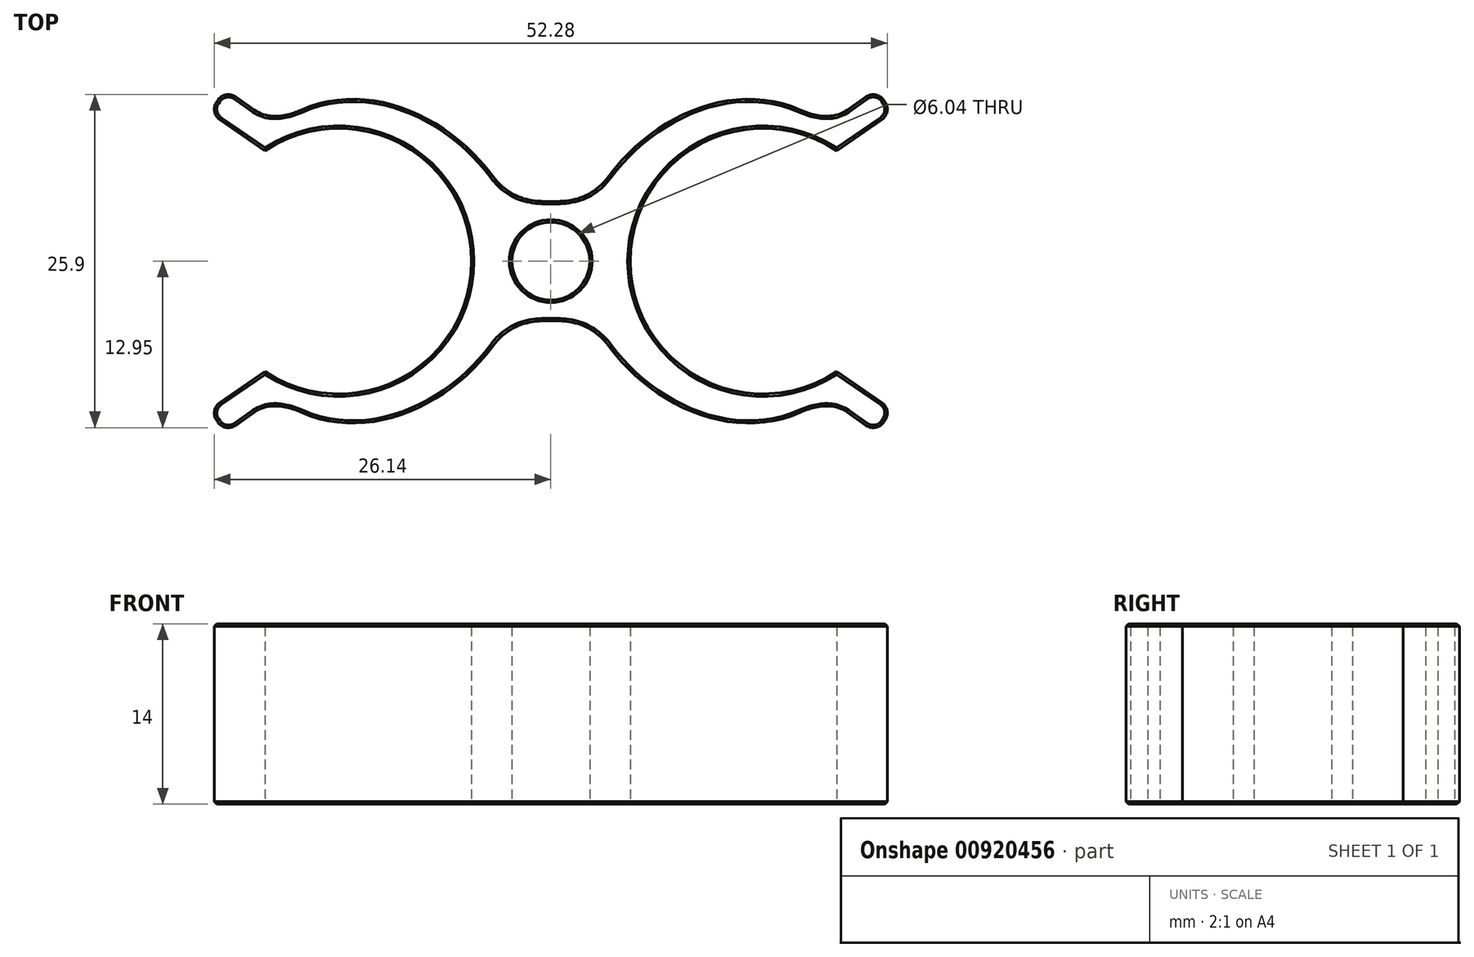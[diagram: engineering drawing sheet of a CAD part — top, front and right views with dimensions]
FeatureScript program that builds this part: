
annotation { "Feature Type Name" : "Feature", "Feature Type Description" : "" }
export const myFeature = defineFeature(function(context is Context, id is Id, definition is map)
    precondition{}
    {
        {
            var Q0;
            Q0=qCreatedBy(makeId("Top.planeOp"),FACE);
            var sketch = newSketch(context, id + "F0", { "sketchPlane" : qUnion([Q0])});
            skLineSegment(sketch, "E0.bottom", {"start": v(-30.7, 16.04) * mm, "end": v(39.3, 16.04) * mm, "construction": true});
            skLineSegment(sketch, "E0.top", {"start": v(-30.7, -18.6) * mm, "end": v(39.3, -18.6) * mm, "construction": true});
            skLineSegment(sketch, "E0.left", {"start": v(-30.7, 16.04) * mm, "end": v(-30.7, -18.6) * mm, "construction": true});
            skLineSegment(sketch, "E0.right", {"start": v(39.3, 16.04) * mm, "end": v(39.3, -18.6) * mm, "construction": true});
            skCircle(sketch, "E1", {"center": v(-16.48, 0) * mm, "radius": 10.32 * mm});
            skLineSegment(sketch, "E2", {"start": v(-26.53, 11.56) * mm, "end": v(-22.21, 8.58) * mm});
            skLineSegment(sketch, "E3", {"start": v(-26.53, 11.56) * mm, "end": v(-25.3, 13.35) * mm});
            skPoint(sketch, "E4.3.internal.snap0", {"position": v(-25.92, 12.45) * mm});
            skFitSpline(sketch, "E5", {"points": [v(-23.04, 11.75) * mm, v(-19.4, 11.75) * mm], "startDerivative": vector(3.9, -2.77) * mm, "endDerivative": vector(1.97, 0.88) * mm});
            skFitSpline(sketch, "E6", {"points": [v(-19.4, 11.75) * mm, v(-4.53, 6.63) * mm], "startDerivative": vector(15.7, 7.01) * mm, "endDerivative": vector(10.41, -14.02) * mm});
            skFitSpline(sketch, "E7", {"points": [v(-4.53, 6.63) * mm, v(0, 4.64) * mm], "startDerivative": vector(4.34, -5.84) * mm, "endDerivative": vector(3.88, 0) * mm});
            skLineSegment(sketch, "E8", {"start": v(-23.04, 11.75) * mm, "end": v(-25.3, 13.35) * mm});
            skLineSegment(sketch, "E9", {"start": v(-41.93, 0) * mm, "end": v(18.12, 0) * mm, "construction": true});
            skLineSegment(sketch, "E10", {"start": v(0, 33.24) * mm, "end": v(0, -36.87) * mm, "construction": true});
            skCircle(sketch, "E11", {"center": v(0, 0) * mm, "radius": 3.02 * mm});
            skLineSegment(sketch, "E12.MirrorCS", {"start": v(26.53, 11.56) * mm, "end": v(22.21, 8.58) * mm});
            skLineSegment(sketch, "E13.MirrorCS", {"start": v(26.53, 11.56) * mm, "end": v(25.3, 13.35) * mm});
            skLineSegment(sketch, "E14.MirrorCS", {"start": v(23.04, 11.75) * mm, "end": v(25.3, 13.35) * mm});
            skFitSpline(sketch, "E15.MirrorCS", {"points": [v(23.04, 11.75) * mm, v(19.4, 11.75) * mm], "startDerivative": vector(-3.9, -2.77) * mm, "endDerivative": vector(-1.97, 0.88) * mm});
            skFitSpline(sketch, "E16.MirrorCS", {"points": [v(19.4, 11.75) * mm, v(4.53, 6.63) * mm], "startDerivative": vector(-15.7, 7.01) * mm, "endDerivative": vector(-10.41, -14.02) * mm});
            skFitSpline(sketch, "E17.MirrorCS", {"points": [v(4.53, 6.63) * mm, v(0, 4.64) * mm], "startDerivative": vector(-4.34, -5.84) * mm, "endDerivative": vector(-3.88, 0) * mm});
            skCircle(sketch, "E18.MirrorC", {"center": v(16.48, 0) * mm, "radius": 10.32 * mm});
            skLineSegment(sketch, "E19.MirrorCS", {"start": v(-26.53, -11.56) * mm, "end": v(-22.21, -8.58) * mm});
            skLineSegment(sketch, "E20.MirrorCS", {"start": v(-26.53, -11.56) * mm, "end": v(-25.3, -13.35) * mm});
            skLineSegment(sketch, "E21.MirrorCS", {"start": v(-23.04, -11.75) * mm, "end": v(-25.3, -13.35) * mm});
            skFitSpline(sketch, "E22.MirrorCS", {"points": [v(-23.04, -11.75) * mm, v(-19.4, -11.75) * mm], "startDerivative": vector(3.9, 2.77) * mm, "endDerivative": vector(1.97, -0.88) * mm});
            skFitSpline(sketch, "E23.MirrorCS", {"points": [v(-19.4, -11.75) * mm, v(-4.53, -6.63) * mm], "startDerivative": vector(15.7, -7.01) * mm, "endDerivative": vector(10.41, 14.02) * mm});
            skFitSpline(sketch, "E24.MirrorCS", {"points": [v(-4.53, -6.63) * mm, v(0, -4.64) * mm], "startDerivative": vector(4.34, 5.84) * mm, "endDerivative": vector(3.88, 0) * mm});
            skFitSpline(sketch, "E25.MirrorCS", {"points": [v(4.53, -6.63) * mm, v(0, -4.64) * mm], "startDerivative": vector(-4.34, 5.84) * mm, "endDerivative": vector(-3.88, 0) * mm});
            skFitSpline(sketch, "E26.MirrorCS", {"points": [v(19.4, -11.75) * mm, v(4.53, -6.63) * mm], "startDerivative": vector(-15.7, -7.01) * mm, "endDerivative": vector(-10.41, 14.02) * mm});
            skFitSpline(sketch, "E27.MirrorCS", {"points": [v(23.04, -11.75) * mm, v(19.4, -11.75) * mm], "startDerivative": vector(-3.9, 2.77) * mm, "endDerivative": vector(-1.97, -0.88) * mm});
            skLineSegment(sketch, "E28.MirrorCS", {"start": v(23.04, -11.75) * mm, "end": v(25.3, -13.35) * mm});
            skLineSegment(sketch, "E29.MirrorCS", {"start": v(26.53, -11.56) * mm, "end": v(25.3, -13.35) * mm});
            skLineSegment(sketch, "E30.MirrorCS", {"start": v(26.53, -11.56) * mm, "end": v(22.21, -8.58) * mm});
            skSolve(sketch);
        }
        {
            var Q0;
            {var subQ4=sQuery(id+"F0.wireOp",EDGE,"E2");Q0=makeQuery(id+"F0.imprint","IMPRINT",FACE,{"disambiguationData":[TD([[makeQuery(id+"F0.imprint","IMPRINT",EDGE,{"derivedFrom":subQ4}),1.0]])]});}
            extrude(context, id + "F1", {"entities" : qUnion([Q0]), "depth" : 14 * mm, "offsetDistance" : 25 * mm});
        }
        {
            var Q0;
            Q0=makeQuery(id+"F1.opExtrude","SWEPT_EDGE",EDGE,{"disambiguationData":[OSD([sQuery(id+"F0.wireOp",EDGE,"E28.MirrorCS"),sQuery(id+"F0.wireOp",EDGE,"E29.MirrorCS")])]});
            var Q1;
            Q1=makeQuery(id+"F1.opExtrude","SWEPT_EDGE",EDGE,{"disambiguationData":[OSD([sQuery(id+"F0.wireOp",EDGE,"E29.MirrorCS"),sQuery(id+"F0.wireOp",EDGE,"E30.MirrorCS")])]});
            var Q2;
            Q2=makeQuery(id+"F1.opExtrude","SWEPT_EDGE",EDGE,{"disambiguationData":[OSD([sQuery(id+"F0.wireOp",EDGE,"E12.MirrorCS"),sQuery(id+"F0.wireOp",EDGE,"E13.MirrorCS")])]});
            var Q3;
            Q3=makeQuery(id+"F1.opExtrude","SWEPT_EDGE",EDGE,{"disambiguationData":[OSD([sQuery(id+"F0.wireOp",EDGE,"E2"),sQuery(id+"F0.wireOp",EDGE,"E3")])]});
            var Q4;
            Q4=makeQuery(id+"F1.opExtrude","SWEPT_EDGE",EDGE,{"disambiguationData":[OSD([sQuery(id+"F0.wireOp",EDGE,"E3"),sQuery(id+"F0.wireOp",EDGE,"E8")])]});
            var Q5;
            Q5=makeQuery(id+"F1.opExtrude","SWEPT_EDGE",EDGE,{"disambiguationData":[OSD([sQuery(id+"F0.wireOp",EDGE,"E20.MirrorCS"),sQuery(id+"F0.wireOp",EDGE,"E21.MirrorCS")])]});
            var Q6;
            Q6=makeQuery(id+"F1.opExtrude","SWEPT_EDGE",EDGE,{"disambiguationData":[OSD([sQuery(id+"F0.wireOp",EDGE,"E19.MirrorCS"),sQuery(id+"F0.wireOp",EDGE,"E20.MirrorCS")])]});
            var Q7;
            Q7=makeQuery(id+"F1.opExtrude","SWEPT_EDGE",EDGE,{"disambiguationData":[OSD([sQuery(id+"F0.wireOp",EDGE,"E13.MirrorCS"),sQuery(id+"F0.wireOp",EDGE,"E14.MirrorCS")])]});
            fillet(context, id + "F2", {"entities" : qUnion([Q0, Q1, Q2, Q3, Q4, Q5, Q6, Q7]), "radius" : 1 * mm, "tangentPropagation" : true, "allowEdgeOverflow" : false});
        }
        {
            var Q0;
            Q0=makeQuery(id+"F1.opExtrude","CAP_FACE",FACE,{"disambiguationData":[OSD([sQuery(id+"F0.wireOp",EDGE,"E1"),sQuery(id+"F0.wireOp",EDGE,"E2"),sQuery(id+"F0.wireOp",EDGE,"E3"),sQuery(id+"F0.wireOp",EDGE,"E5"),sQuery(id+"F0.wireOp",EDGE,"E6"),sQuery(id+"F0.wireOp",EDGE,"E7"),sQuery(id+"F0.wireOp",EDGE,"E8"),sQuery(id+"F0.wireOp",EDGE,"E11"),sQuery(id+"F0.wireOp",EDGE,"E12.MirrorCS"),sQuery(id+"F0.wireOp",EDGE,"E13.MirrorCS"),sQuery(id+"F0.wireOp",EDGE,"E14.MirrorCS"),sQuery(id+"F0.wireOp",EDGE,"E15.MirrorCS"),sQuery(id+"F0.wireOp",EDGE,"E16.MirrorCS"),sQuery(id+"F0.wireOp",EDGE,"E17.MirrorCS"),sQuery(id+"F0.wireOp",EDGE,"E18.MirrorC"),sQuery(id+"F0.wireOp",EDGE,"E19.MirrorCS"),sQuery(id+"F0.wireOp",EDGE,"E20.MirrorCS"),sQuery(id+"F0.wireOp",EDGE,"E21.MirrorCS"),sQuery(id+"F0.wireOp",EDGE,"E22.MirrorCS"),sQuery(id+"F0.wireOp",EDGE,"E23.MirrorCS"),sQuery(id+"F0.wireOp",EDGE,"E24.MirrorCS"),sQuery(id+"F0.wireOp",EDGE,"E25.MirrorCS"),sQuery(id+"F0.wireOp",EDGE,"E26.MirrorCS"),sQuery(id+"F0.wireOp",EDGE,"E27.MirrorCS"),sQuery(id+"F0.wireOp",EDGE,"E28.MirrorCS"),sQuery(id+"F0.wireOp",EDGE,"E29.MirrorCS"),sQuery(id+"F0.wireOp",EDGE,"E30.MirrorCS")])],"isStart":false});
            var Q1;
            Q1=makeQuery(id+"F1.opExtrude","CAP_FACE",FACE,{"disambiguationData":[OSD([sQuery(id+"F0.wireOp",EDGE,"E1"),sQuery(id+"F0.wireOp",EDGE,"E2"),sQuery(id+"F0.wireOp",EDGE,"E3"),sQuery(id+"F0.wireOp",EDGE,"E5"),sQuery(id+"F0.wireOp",EDGE,"E6"),sQuery(id+"F0.wireOp",EDGE,"E7"),sQuery(id+"F0.wireOp",EDGE,"E8"),sQuery(id+"F0.wireOp",EDGE,"E11"),sQuery(id+"F0.wireOp",EDGE,"E12.MirrorCS"),sQuery(id+"F0.wireOp",EDGE,"E13.MirrorCS"),sQuery(id+"F0.wireOp",EDGE,"E14.MirrorCS"),sQuery(id+"F0.wireOp",EDGE,"E15.MirrorCS"),sQuery(id+"F0.wireOp",EDGE,"E16.MirrorCS"),sQuery(id+"F0.wireOp",EDGE,"E17.MirrorCS"),sQuery(id+"F0.wireOp",EDGE,"E18.MirrorC"),sQuery(id+"F0.wireOp",EDGE,"E19.MirrorCS"),sQuery(id+"F0.wireOp",EDGE,"E20.MirrorCS"),sQuery(id+"F0.wireOp",EDGE,"E21.MirrorCS"),sQuery(id+"F0.wireOp",EDGE,"E22.MirrorCS"),sQuery(id+"F0.wireOp",EDGE,"E23.MirrorCS"),sQuery(id+"F0.wireOp",EDGE,"E24.MirrorCS"),sQuery(id+"F0.wireOp",EDGE,"E25.MirrorCS"),sQuery(id+"F0.wireOp",EDGE,"E26.MirrorCS"),sQuery(id+"F0.wireOp",EDGE,"E27.MirrorCS"),sQuery(id+"F0.wireOp",EDGE,"E28.MirrorCS"),sQuery(id+"F0.wireOp",EDGE,"E29.MirrorCS"),sQuery(id+"F0.wireOp",EDGE,"E30.MirrorCS")])],"isStart":true});
            chamfer(context, id + "F3", {"entities" : qUnion([Q0, Q1]), "width" : 0.2 * mm, "tangentPropagation" : true});
        }
    });
